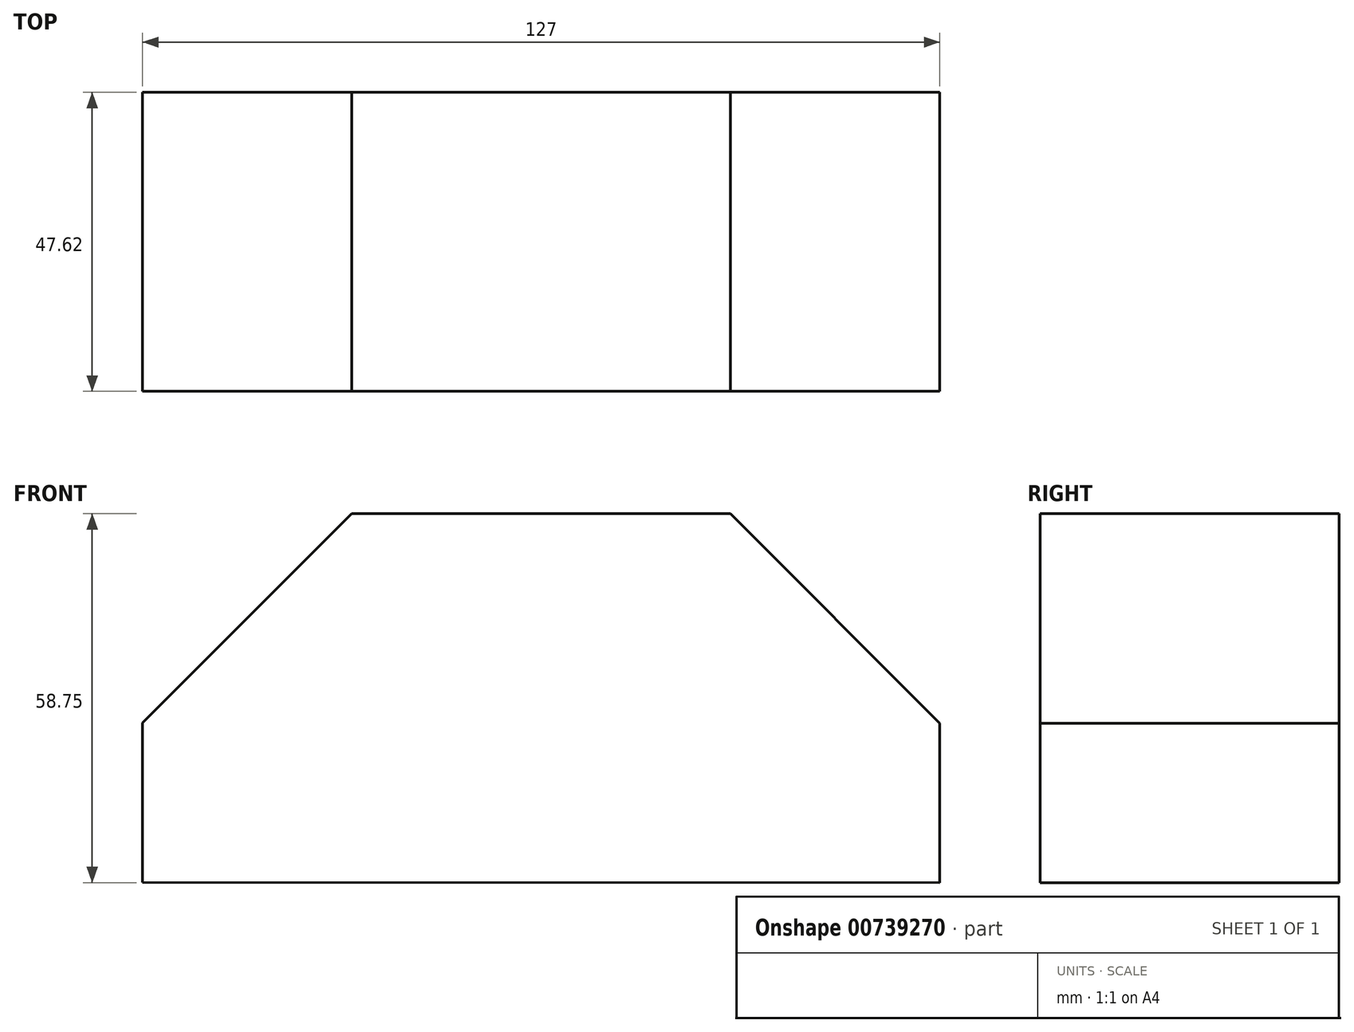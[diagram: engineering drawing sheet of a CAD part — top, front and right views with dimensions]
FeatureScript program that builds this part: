
annotation { "Feature Type Name" : "Feature", "Feature Type Description" : "" }
export const myFeature = defineFeature(function(context is Context, id is Id, definition is map)
    precondition{}
    {
        {
            var Q0;
            Q0=qCreatedBy(makeId("Front.planeOp"),FACE);
            var sketch = newSketch(context, id + "F0", { "sketchPlane" : qUnion([Q0])});
            skLineSegment(sketch, "E0", {"start": v(-57.46, -30.44) * mm, "end": v(-57.46, -5.04) * mm});
            skLineSegment(sketch, "E1", {"start": v(-57.46, -5.04) * mm, "end": v(-24.11, 28.3) * mm});
            skLineSegment(sketch, "E2", {"start": v(-24.11, 28.3) * mm, "end": v(36.19, 28.3) * mm});
            skLineSegment(sketch, "E3", {"start": v(36.19, 28.3) * mm, "end": v(69.54, -5.05) * mm});
            skLineSegment(sketch, "E4", {"start": v(69.54, -5.05) * mm, "end": v(69.54, -30.45) * mm});
            skLineSegment(sketch, "E5", {"start": v(69.54, -30.45) * mm, "end": v(-57.46, -30.44) * mm});
            skSolve(sketch);
        }
        {
            var Q0;
            Q0=makeQuery(id+"F0.imprint","IMPRINT",FACE,{"disambiguationData":[TD([[makeQuery(id+"F0.imprint","IMPRINT",EDGE,{"derivedFrom":sQuery(id+"F0.wireOp",EDGE,"E0")}),-1.0]])]});
            extrude(context, id + "F1", {"entities" : qUnion([Q0]), "depth" : 47.62 * mm, "offsetDistance" : 25.4 * mm});
        }
    });
